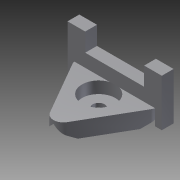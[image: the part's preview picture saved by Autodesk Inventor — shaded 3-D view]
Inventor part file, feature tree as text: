
AUTODESK INVENTOR PART (.ipt)
format: ipt  version: 2011 (Build 150239000, 239)  size: 201,216 bytes
history: native  units: in
note: dims shown in document units (in); Inventor stores cm internally (conversion verified against a paired STEP export)
features: sketch x7, extrude x6, other x1, imported_body x1, hole x1
ambient origin geometry x8: Origin, YZ Plane, XZ Plane, XY Plane, X Axis, Y Axis, Z Axis, Center Point
feature tree (16):
  other  "TricornerGround"
  imported_body  "Base1"
  extrude  "Extrusion1"  Depth=0.1181in
  hole  "Hole1"  [1 undecoded]
  extrude  "Extrusion2"  Depth=0.4724in
  extrude  "Extrusion3"  Depth=0.1181in
  extrude  "Extrusion4"  Depth=0.2953in
  extrude  "Extrusion5"  Depth=0.1839in TaperAngle=0.0deg
  extrude  "Extrusion6"  Depth=0.1575in TaperAngle=0.0deg
  sketch  "Sketch2"  dims[d0=0.1575in d1=0.0in d2=0.1181in]
  sketch  "Sketch3"  dims[d3=0.1181in d4=0.2362in d5=0.1575in d6=0.0787in d7=90.0deg d8=0.315in d9=0.8108in d10=0.3346in]
  sketch  "Sketch4"  dims[d11=0.1181in d12=0.0in d13=0.4724in]
  sketch  "Sketch5"  dims[d14=0.9449in d15=0.1181in]
  sketch  "Sketch6"  dims[d16=0.315in d17=0.0in d18=0.2953in]
  sketch  "Sketch7"  dims[d19=0.5906in d20=0.1839in d21=0.0in]
  sketch  "Sketch8"  dims[d22=0.1575in d23=0.0in d24=0.1575in d25=0.0in]
note: 1 required parameter value undecoded (feature->parameter linkage not recoverable at this tier; creation-order binding heuristic only, values carry confidence <= 0.55)
